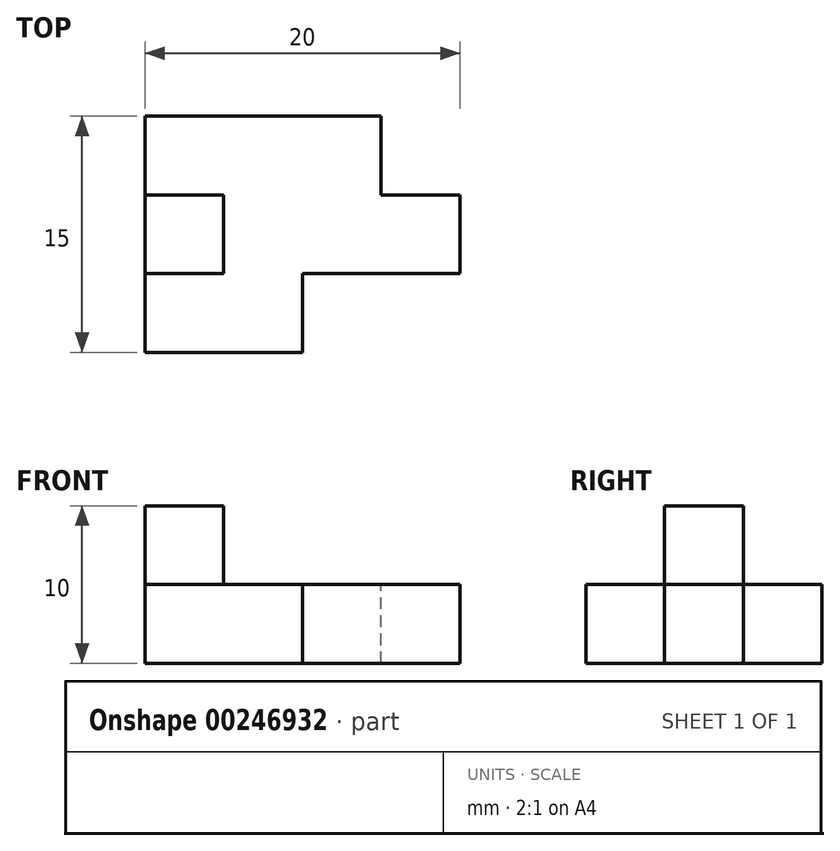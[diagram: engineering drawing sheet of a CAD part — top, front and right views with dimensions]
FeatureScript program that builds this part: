
annotation { "Feature Type Name" : "Feature", "Feature Type Description" : "" }
export const myFeature = defineFeature(function(context is Context, id is Id, definition is map)
    precondition{}
    {
        {
            var Q0;
            Q0=qCreatedBy(makeId("Front.planeOp"),FACE);
            var sketch = newSketch(context, id + "F0", { "sketchPlane" : qUnion([Q0])});
            skLineSegment(sketch, "E0.bottom", {"start": v(0, 0) * mm, "end": v(5, 0) * mm});
            skLineSegment(sketch, "E0.top", {"start": v(0, 10) * mm, "end": v(5, 10) * mm});
            skLineSegment(sketch, "E0.left", {"start": v(0, 0) * mm, "end": v(0, 10) * mm});
            skLineSegment(sketch, "E0.right", {"start": v(5, 0) * mm, "end": v(5, 10) * mm});
            skLineSegment(sketch, "E1.bottom", {"start": v(0, 0) * mm, "end": v(20, 0) * mm});
            skLineSegment(sketch, "E1.top", {"start": v(0, 5) * mm, "end": v(20, 5) * mm});
            skLineSegment(sketch, "E1.left", {"start": v(0, 0) * mm, "end": v(0, 5) * mm});
            skLineSegment(sketch, "E1.right", {"start": v(20, 0) * mm, "end": v(20, 5) * mm});
            skLineSegment(sketch, "E2", {"start": v(10, 5) * mm, "end": v(10, 0) * mm});
            skSolve(sketch);
        }
        {
            var Q0;
            Q0 = qSketchRegion(id + "F0", true);
            extrude(context, id + "F1", {"entities" : qUnion([Q0]), "depth" : 15 * mm});
        }
        {
            var Q0;
            {var subQ0=sQuery(id+"F0.wireOp",EDGE,"E0.top");Q0=makeQuery(id+"F0.imprint","IMPRINT",FACE,{"disambiguationData":[TD([[makeQuery(id+"F0.imprint","IMPRINT",EDGE,{"derivedFrom":subQ0}),-1.0]])]});}
            extrude(context, id + "F2", {"entities" : qUnion([Q0]), "operationType" : NewBodyOperationType.REMOVE, "depth" : 5 * mm});
        }
        {
            var Q0;
            Q0=makeQuery(id+"F1.opExtrude","SWEPT_FACE",FACE,{"disambiguationData":[OSD([sQuery(id+"F0.wireOp",EDGE,"E0.right")])]});
            var sketch = newSketch(context, id + "F3", { "sketchPlane" : qUnion([Q0])});
            skLineSegment(sketch, "E3", {"start": v(-10, 10) * mm, "end": v(-10, 5) * mm});
            skLineSegment(sketch, "E4", {"start": v(-10, 5) * mm, "end": v(-15, 5) * mm});
            skLineSegment(sketch, "E5", {"start": v(-15, 5) * mm, "end": v(-15, 10) * mm});
            skLineSegment(sketch, "E6", {"start": v(-15, 10) * mm, "end": v(-10, 10) * mm});
            skSolve(sketch);
        }
        {
            var Q0;
            Q0=makeQuery(id+"F3.imprint","IMPRINT",FACE,{"disambiguationData":[TD([[makeQuery(id+"F3.imprint","IMPRINT",EDGE,{"derivedFrom":sQuery(id+"F3.wireOp",EDGE,"E3")}),-1.0]])]});
            extrude(context, id + "F4", {"entities" : qUnion([Q0]), "operationType" : NewBodyOperationType.REMOVE, "oppositeDirection" : true, "depth" : 5 * mm});
        }
        {
            var Q0;
            {var subQ0=sQuery(id+"F0.wireOp",EDGE,"E1.top");Q0=makeQuery(id+"F4.boolean.opBoolean","MERGE",FACE,{"derivedFrom":[makeQuery(id+"F2.boolean.opBoolean","MERGE",FACE,{"derivedFrom":[makeQuery(id+"F1.opExtrude","SWEPT_FACE",FACE,{"disambiguationData":[OSD([subQ0])]}),makeQuery(id+"F2.opExtrude","SWEPT_FACE",FACE,{"disambiguationData":[OSD([subQ0])]})]}),makeQuery(id+"F4.opExtrude","SWEPT_FACE",FACE,{"disambiguationData":[OSD([sQuery(id+"F3.wireOp",EDGE,"E4")])]})]});}
            var sketch = newSketch(context, id + "F5", { "sketchPlane" : qUnion([Q0])});
            skLineSegment(sketch, "E7", {"start": v(5, -10) * mm, "end": v(20, -10) * mm});
            skLineSegment(sketch, "E8", {"start": v(5, -10) * mm, "end": v(5, -15) * mm});
            skLineSegment(sketch, "E9", {"start": v(5, -15) * mm, "end": v(10, -15) * mm});
            skLineSegment(sketch, "E10", {"start": v(10, -15) * mm, "end": v(10, -10) * mm});
            skLineSegment(sketch, "E11", {"start": v(10, -15) * mm, "end": v(20, -15) * mm});
            skLineSegment(sketch, "E12", {"start": v(20, -15) * mm, "end": v(20, -10) * mm});
            skLineSegment(sketch, "E13", {"start": v(5, -5) * mm, "end": v(20, -5) * mm});
            skLineSegment(sketch, "E14", {"start": v(20, -5) * mm, "end": v(20, 0) * mm});
            skLineSegment(sketch, "E15", {"start": v(20, 0) * mm, "end": v(15, 0) * mm});
            skLineSegment(sketch, "E16", {"start": v(15, 0) * mm, "end": v(15, -5) * mm});
            skSolve(sketch);
        }
        {
            var Q0;
            {var subQ2=sQuery(id+"F5.wireOp",EDGE,"E10");Q0=makeQuery(id+"F5.imprint","IMPRINT",FACE,{"disambiguationData":[TD([[makeQuery(id+"F5.imprint","IMPRINT",EDGE,{"derivedFrom":subQ2}),-1.0]])]});}
            extrude(context, id + "F6", {"entities" : qUnion([Q0]), "operationType" : NewBodyOperationType.REMOVE, "oppositeDirection" : true, "depth" : 5 * mm});
        }
        {
            var Q0;
            {var subQ0=sQuery(id+"F5.wireOp",EDGE,"E14");Q0=makeQuery(id+"F5.imprint","IMPRINT",FACE,{"disambiguationData":[TD([[makeQuery(id+"F5.imprint","IMPRINT",EDGE,{"derivedFrom":subQ0}),1.0]])]});}
            extrude(context, id + "F7", {"entities" : qUnion([Q0]), "operationType" : NewBodyOperationType.REMOVE, "oppositeDirection" : true, "depth" : 5 * mm});
        }
    });
